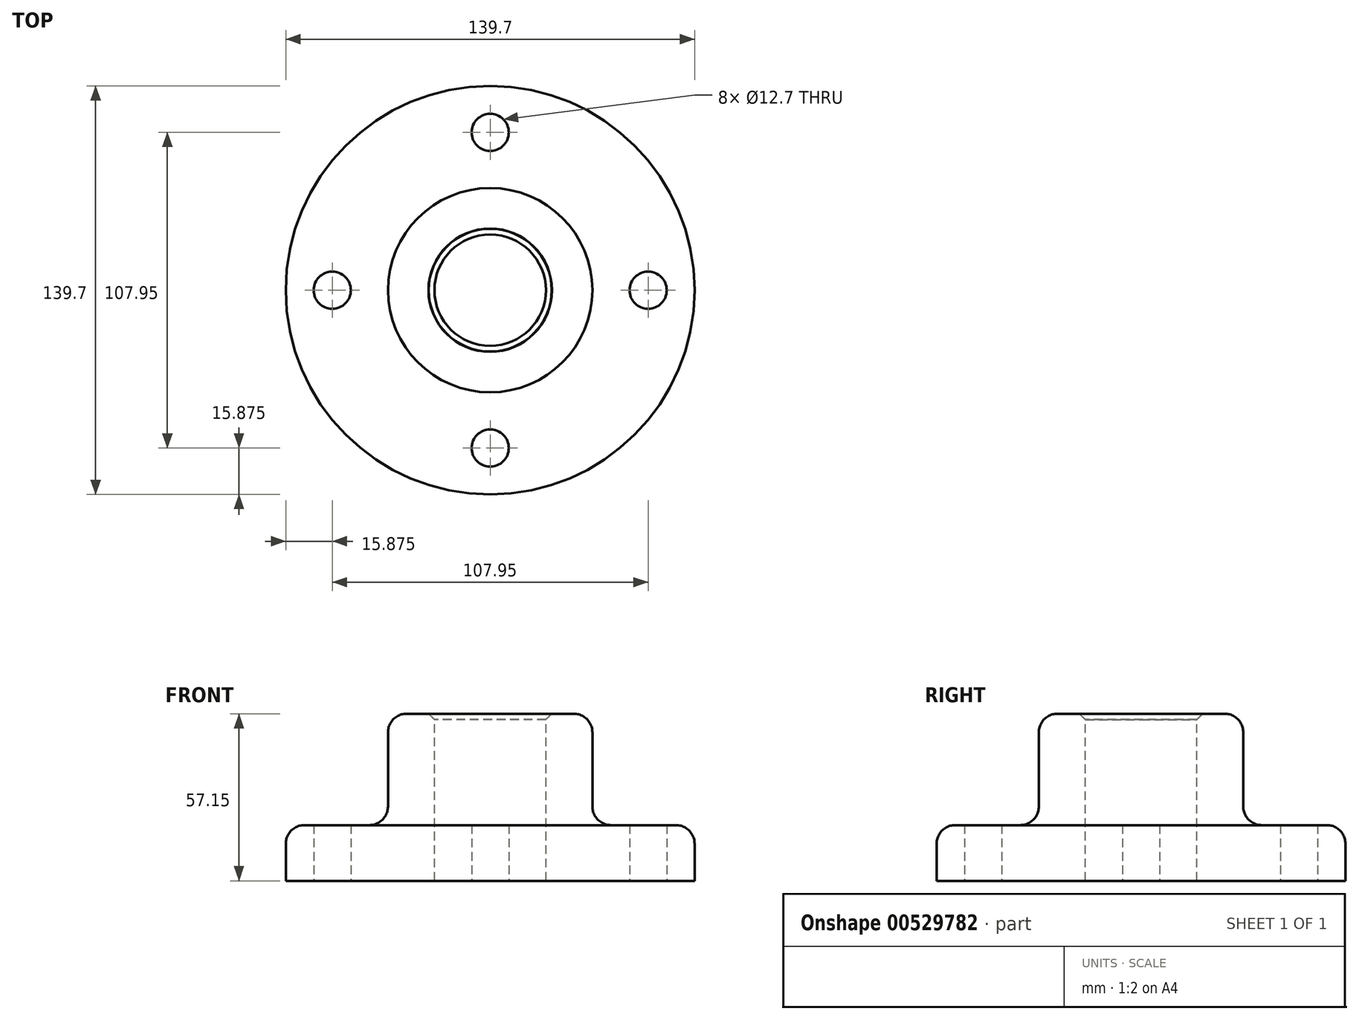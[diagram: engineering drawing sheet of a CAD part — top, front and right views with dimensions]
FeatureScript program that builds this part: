
annotation { "Feature Type Name" : "Feature", "Feature Type Description" : "" }
export const myFeature = defineFeature(function(context is Context, id is Id, definition is map)
    precondition{}
    {
        {
            var Q0;
            Q0=qCreatedBy(makeId("Front.planeOp"),FACE);
            var sketch = newSketch(context, id + "F0", { "sketchPlane" : qUnion([Q0])});
            skLineSegment(sketch, "E0.bottom", {"start": v(-63.5, -27.63) * mm, "end": v(-41.27, -27.63) * mm});
            skLineSegment(sketch, "E0.top", {"start": v(-69.85, -46.68) * mm, "end": v(69.85, -46.68) * mm});
            skLineSegment(sketch, "E0.left", {"start": v(-69.85, -33.98) * mm, "end": v(-69.85, -46.68) * mm});
            skLineSegment(sketch, "E0.right", {"start": v(69.85, -33.98) * mm, "end": v(69.85, -46.68) * mm});
            skLineSegment(sketch, "E1.bottom", {"start": v(-28.57, 10.47) * mm, "end": v(28.58, 10.47) * mm});
            skLineSegment(sketch, "E1.top", {"start": v(-19.05, -46.68) * mm, "end": v(19.05, -46.68) * mm});
            skLineSegment(sketch, "E1.left", {"start": v(-34.92, 4.12) * mm, "end": v(-34.92, -21.28) * mm});
            skLineSegment(sketch, "E1.right", {"start": v(34.93, 4.12) * mm, "end": v(34.93, -21.28) * mm});
            skLineSegment(sketch, "E2.bottom", {"start": v(-19.05, 10.47) * mm, "end": v(19.05, 10.47) * mm});
            skLineSegment(sketch, "E2.left", {"start": v(-19.05, 8.44) * mm, "end": v(-19.05, -46.68) * mm});
            skLineSegment(sketch, "E2.right", {"start": v(19.05, 8.52) * mm, "end": v(19.05, -46.68) * mm});
            skLineSegment(sketch, "E3.trimOffspring", {"start": v(41.28, -27.63) * mm, "end": v(63.5, -27.63) * mm});
            skLineSegment(sketch, "E4", {"start": v(-21.08, 47.6) * mm, "end": v(-21.08, -60.53) * mm, "construction": true});
            skLineSegment(sketch, "E5", {"start": v(21.08, 44.6) * mm, "end": v(21.08, -59.86) * mm, "construction": true});
            skLineSegment(sketch, "E6", {"start": v(-21.08, 10.47) * mm, "end": v(-19.05, 8.44) * mm});
            skLineSegment(sketch, "E7", {"start": v(21, 10.47) * mm, "end": v(19.05, 8.52) * mm});
            skPoint(sketch, "E8.visualSharp", {"position": v(-34.92, 10.47) * mm});
            skArc(sketch, "E8.filletArc", {"start": v(-28.57, 10.47) * mm, "mid": v(-33.07, 8.61) * mm, "end": v(-34.92, 4.12) * mm});
            skPoint(sketch, "E9.visualSharp", {"position": v(34.93, 10.47) * mm});
            skArc(sketch, "E9.filletArc", {"start": v(34.93, 4.12) * mm, "mid": v(33.07, 8.61) * mm, "end": v(28.58, 10.47) * mm});
            skPoint(sketch, "E10.visualSharp", {"position": v(-34.92, -27.63) * mm});
            skArc(sketch, "E10.filletArc", {"start": v(-41.27, -27.63) * mm, "mid": v(-36.78, -25.77) * mm, "end": v(-34.92, -21.28) * mm});
            skPoint(sketch, "E11.visualSharp", {"position": v(34.93, -27.63) * mm});
            skArc(sketch, "E11.filletArc", {"start": v(34.93, -21.28) * mm, "mid": v(36.78, -25.77) * mm, "end": v(41.28, -27.63) * mm});
            skPoint(sketch, "E12.visualSharp", {"position": v(-69.85, -27.63) * mm});
            skArc(sketch, "E12.filletArc", {"start": v(-63.5, -27.63) * mm, "mid": v(-68, -29.49) * mm, "end": v(-69.85, -33.98) * mm});
            skPoint(sketch, "E13.visualSharp", {"position": v(69.85, -27.63) * mm});
            skArc(sketch, "E13.filletArc", {"start": v(69.85, -33.98) * mm, "mid": v(68, -29.49) * mm, "end": v(63.5, -27.63) * mm});
            skLineSegment(sketch, "E14", {"start": v(0, 51.97) * mm, "end": v(0, -80.45) * mm, "construction": true});
            skSolve(sketch);
        }
        {
            var Q0;
            Q0=makeQuery(id+"F0.imprint","IMPRINT",FACE,{"disambiguationData":[TD([[makeQuery(id+"F0.imprint","IMPRINT",EDGE,{"derivedFrom":sQuery(id+"F0.wireOp",EDGE,"E0.bottom")}),-1.0]])]});
            var Q1;
            {var subQ3=sQuery(id+"F0.wireOp",EDGE,"E0.right");Q1=makeQuery(id+"F0.imprint","IMPRINT",FACE,{"disambiguationData":[TD([[makeQuery(id+"F0.imprint","IMPRINT",EDGE,{"derivedFrom":subQ3}),-1.0]])]});}
            var Q2;
            Q2=sQuery(id+"F0.wireOp",EDGE,"E14");
            revolve(context, id + "F1", {"entities" : qUnion([Q0, Q1]), "axis" : qUnion([Q2]), "revolveType" : RevolveType.FULL});
        }
        {
            var Q0;
            {var subQ0=sQuery(id+"F0.wireOp",EDGE,"E0.top");Q0=makeQuery(id+"F1.opRevolve","SWEPT_FACE",FACE,{"disambiguationData":[OSD([subQ0]),TDD([makeQuery(id+"F0.imprint","IMPRINT",EDGE,{"disambiguationData":[TD([[makeQuery(id+"F0.imprint","INTERSECT",VERTEX,{"derivedFrom":[subQ0,sQuery(id+"F0.wireOp",EDGE,"E0.left")]}),-1.0]])],"derivedFrom":subQ0})])]});}
            var sketch = newSketch(context, id + "F2", { "sketchPlane" : qUnion([Q0])});
            skLineSegment(sketch, "E15", {"start": v(0, 86.3) * mm, "end": v(0, -86.03) * mm, "construction": true});
            skLineSegment(sketch, "E16", {"start": v(85.49, 0) * mm, "end": v(-85.76, 0) * mm, "construction": true});
            skCircle(sketch, "E17", {"center": v(0, 53.97) * mm, "radius": 6.35 * mm});
            skCircle(sketch, "E18.1.0", {"center": v(-53.97, 0) * mm, "radius": 6.35 * mm});
            skCircle(sketch, "E18.2.0", {"center": v(0, -53.97) * mm, "radius": 6.35 * mm});
            skCircle(sketch, "E18.3.0", {"center": v(53.97, 0) * mm, "radius": 6.35 * mm});
            skPoint(sketch, "E18.center", {"position": v(0, 0) * mm});
            skSolve(sketch);
        }
        {
            var Q0;
            Q0=makeQuery(id+"F2.imprint","IMPRINT",FACE,{"disambiguationData":[TD([[makeQuery(id+"F2.imprint","IMPRINT",EDGE,{"derivedFrom":sQuery(id+"F2.wireOp",EDGE,"E17")}),1.0]])]});
            var Q1;
            Q1=makeQuery(id+"F2.imprint","IMPRINT",FACE,{"disambiguationData":[TD([[makeQuery(id+"F2.imprint","IMPRINT",EDGE,{"derivedFrom":sQuery(id+"F2.wireOp",EDGE,"E18.3.0")}),1.0]])]});
            var Q2;
            Q2=makeQuery(id+"F2.imprint","IMPRINT",FACE,{"disambiguationData":[TD([[makeQuery(id+"F2.imprint","IMPRINT",EDGE,{"derivedFrom":sQuery(id+"F2.wireOp",EDGE,"E18.1.0")}),1.0]])]});
            var Q3;
            Q3=makeQuery(id+"F2.imprint","IMPRINT",FACE,{"disambiguationData":[TD([[makeQuery(id+"F2.imprint","IMPRINT",EDGE,{"derivedFrom":sQuery(id+"F2.wireOp",EDGE,"E18.2.0")}),1.0]])]});
            extrude(context, id + "F3", {"entities" : qUnion([Q0, Q1, Q2, Q3]), "operationType" : NewBodyOperationType.REMOVE, "oppositeDirection" : true, "depth" : 25.4 * mm, "offsetDistance" : 25.4 * mm});
        }
    });
